# Revit family: Bath-Drop_In-KALLISTA-Perfect-P50045
name_source: partatom
category: Plumbing Fixtures
units: mm (PartAtom-declared; Revit-internal decimal feet)

## family parameters
Cut with Voids When Loaded = No
Host = Face
Maintain Annotation Orientation = No
OmniClass Number = 23.31.15.00
OmniClass Title = Bathtubs
Part Type = Normal
Room Calculation Point = No
Round Connector Dimension = Use Diameter
Shared = No

## types (4) — shared parameters
ADA Compliant = No
Assembly Code = D2010500
CW Connection = No
Cold Water Inlet = Cold Water Inlet
Date Modified = 06/07/2025
Default Elevation = 0"
Drain Included = No
HW Connection = No
Height = 24"
Hot Water Inlet = Hot Water Inlet
Length = 69"
Manufacturer = Kallista  Co.
Master Format 2014 = 22 41 19
Master Format 2014 Name = Residential Bathtubs
Material = Cast Stone
Product Name = Perfect
URL = https://www.kallista.com
Vent Connection = No
Waste Connection = Yes
Waste Water Outlet = Waste Water Outlet
WaterSense Certified = No
Width = 37"

## per-type parameters (varying)
| type | Description | Finish | G5 | Model | Product Documentation Link | Product Page URL | Type |
| 0-White | Large Rectangular Bathtub | Kallista-Cast_Stone-0-White | No | P50045-00-0 | https://techcomm.kohler.com | https://www.kallista.com | 1 |
| 96-Biscuit | Large Rectangular Bathtub | Kallista-Vitreous_China-96-Biscuit | No | P50045-00-96 |  |  | 2 |
| G5, 0-White | Large Rectangular Air Bathtub | Kallista-Cast_Stone-0-White | Yes | P50045-G5-0 | https://techcomm.kohler.com | https://www.kallista.com | 3 |
| G5, 96-Biscuit | Large Rectangular Air Bathtub | Kallista-Vitreous_China-96-Biscuit | Yes | P50045-G5-96 |  |  | 4 |

## geometry (parser evidence)
native form markers: Sweep x5
no freeform markers — native parametric forms only
